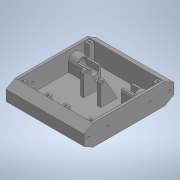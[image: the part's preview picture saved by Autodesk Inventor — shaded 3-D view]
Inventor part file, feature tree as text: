
AUTODESK INVENTOR PART (.ipt)
format: ipt  version: 2020 (Build 240168000, 168)  size: 373,760 bytes
history: native  units: in
note: dims shown in document units (in); Inventor stores cm internally (conversion verified against a paired STEP export)
features: projected_geometry x13, extrude x11, sketch x11, mirror x4, plane x1
ambient origin geometry x8: Origin, YZ Plane, XZ Plane, XY Plane, X Axis, Y Axis, Z Axis, Center Point
bodies: Solid1 (feature_tree)
feature tree (40):
  extrude  "Extrusion1"  Depth=5.9055in
  extrude  "Extrusion2"  TaperAngle=0.0deg  [1 undecoded]
  extrude  "Extrusion3"  Depth=1.2598in
  extrude  "Extrusion4"  Depth=0.315in
  extrude  "Extrusion5"  TaperAngle=0.0deg  [1 undecoded]
  extrude  "Extrusion6"  Depth=0.689in
  mirror  "Mirror1"
  extrude  "Extrusion7"  Depth=0.0787in
  mirror  "Mirror2"
  extrude  "Extrusion8"  Depth=0.5512in
  mirror  "Mirror3"
  plane  "Work Plane1"
  extrude  "Extrusion9"  Depth=0.7874in TaperAngle=0.0deg
  mirror  "Mirror4"
  extrude  "Extrusion10"  Depth=6.063in TaperAngle=0.0deg
  extrude  "Extrusion11"  Depth=0.1575in
  sketch  "Sketch1"  dims[d0=1.378in d1=5.9055in]
  sketch  "Sketch2"  dims[d2=5.1181in d3=0.0in]
  projected_geometry  "Projected Loop1"
  sketch  "Sketch3"  dims[d4=0.1575in d5=1.2598in]
  projected_geometry  "Projected Loop2"
  projected_geometry  "Projected Loop3"
  sketch  "Sketch4"  dims[d6=0.0in d8=0.315in]
  sketch  "Sketch5"  dims[d10=1.1898in d11=0.0in]
  projected_geometry  "Projected Loop4"
  sketch  "Sketch6"  dims[d12=0.6496in d13=0.689in]
  sketch  "Sketch7"  dims[d14=1.5748in d15=0.0787in]
  sketch  "Sketch9"  dims[d16=0.5512in d17=0.0in d18=0.6102in]
  sketch  "Sketch10"  dims[d19=0.4803in d20=0.7874in d21=0.0in]
  sketch  "Sketch12"  dims[d22=0.1654in d23=6.063in d24=0.0in]
  projected_geometry  "Projected Loop6"
  projected_geometry  "Projected Loop7"
  projected_geometry  "Projected Loop8"
  sketch  "Sketch13"  dims[d25=0.5967in d26=0.1575in d27=1.5748in d28=0.0in d29=0.0in d30=0.1575in d31=0.2756in d32=0.0in d33=0.4331in d34=0.122in d38=2.7559in d40=0.061in d41=0.0787in d42=0.2362in d43=0.0in d44=60.0deg d45=0.0787in d46=0.315in d48=1.1898in d49=0.0in d51=0.1575in d52=0.1575in d53=0.2756in d54=0.0in]
  projected_geometry  "Projected Loop9"
  projected_geometry  "Projected Loop10"
  projected_geometry  "Projected Loop11"
  projected_geometry  "Projected Loop12"
  projected_geometry  "Projected Loop13"
  projected_geometry  "Projected Loop14"
note: 2 required parameter values undecoded (feature->parameter linkage not recoverable at this tier; creation-order binding heuristic only, values carry confidence <= 0.55)
